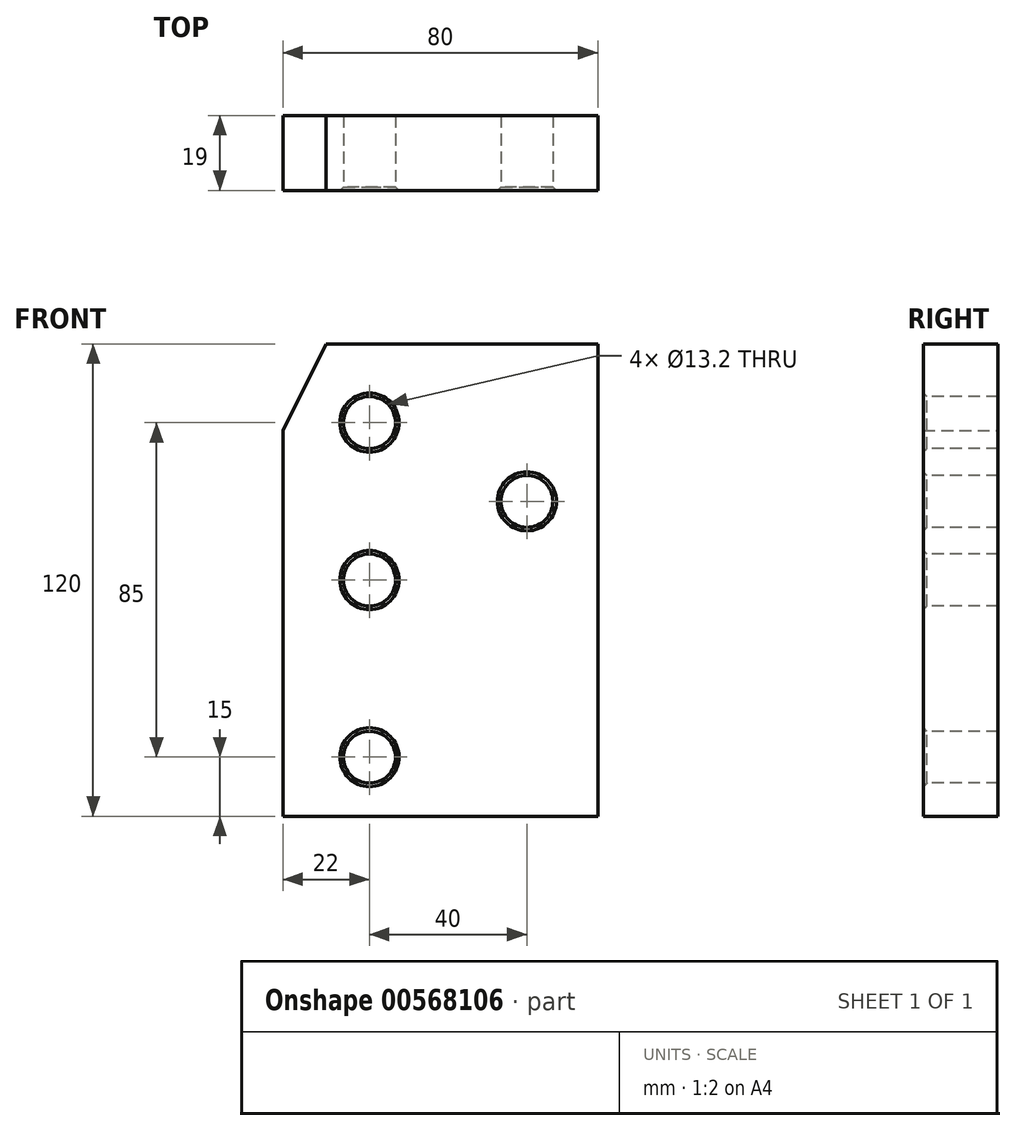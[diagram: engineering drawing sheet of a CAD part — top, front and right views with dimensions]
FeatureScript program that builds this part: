
annotation { "Feature Type Name" : "Feature", "Feature Type Description" : "" }
export const myFeature = defineFeature(function(context is Context, id is Id, definition is map)
    precondition{}
    {
        {
            var Q0;
            Q0=qCreatedBy(makeId("Front.planeOp"),FACE);
            var sketch = newSketch(context, id + "F0", { "sketchPlane" : qUnion([Q0])});
            skLineSegment(sketch, "E0.bottom", {"start": v(0, 0) * mm, "end": v(80, 0) * mm});
            skLineSegment(sketch, "E0.top", {"start": v(11, 120) * mm, "end": v(80, 120) * mm});
            skLineSegment(sketch, "E0.left", {"start": v(0, 0) * mm, "end": v(0, 98) * mm});
            skLineSegment(sketch, "E0.right", {"start": v(80, 0) * mm, "end": v(80, 120) * mm});
            skPoint(sketch, "E1", {"position": v(11, 120) * mm});
            skPoint(sketch, "E2", {"position": v(0, 98) * mm});
            skLineSegment(sketch, "E3", {"start": v(0, 98) * mm, "end": v(11, 120) * mm});
            skPoint(sketch, "E4.orphan", {"position": v(0, 120) * mm});
            skSolve(sketch);
        }
        {
            var Q0;
            Q0 = qSketchRegion(id + "F0", true);
            var Q1;
            Q1=makeQuery(id+"F0.imprint","IMPRINT",FACE,{"disambiguationData":[TD([[makeQuery(id+"F0.imprint","IMPRINT",EDGE,{"derivedFrom":sQuery(id+"F0.wireOp",EDGE,"E0.bottom")}),1.0]])]});
            extrude(context, id + "F1", {"entities" : qUnion([Q0, Q1]), "depth" : 19 * mm, "offsetDistance" : 25 * mm});
        }
        {
            var Q0;
            Q0=makeQuery(id+"F1.opExtrude","CAP_FACE",FACE,{"disambiguationData":[OSD([sQuery(id+"F0.wireOp",EDGE,"E0.bottom"),sQuery(id+"F0.wireOp",EDGE,"E0.top"),sQuery(id+"F0.wireOp",EDGE,"E0.left"),sQuery(id+"F0.wireOp",EDGE,"E0.right")])],"isStart":false});
            var sketch = newSketch(context, id + "F2", { "sketchPlane" : qUnion([Q0])});
            skPoint(sketch, "E5", {"position": v(22, 15) * mm});
            skPoint(sketch, "E6", {"position": v(22, 60) * mm});
            skPoint(sketch, "E7", {"position": v(22, 100) * mm});
            skPoint(sketch, "E8", {"position": v(62, 80) * mm});
            skSolve(sketch);
        }
        {
            var Q0;
            Q0=sQuery(id+"F2.wireOp",VERTEX,"E8");
            var Q1;
            Q1=sQuery(id+"F2.wireOp",VERTEX,"E5");
            var Q2;
            Q2=sQuery(id+"F2.wireOp",VERTEX,"E6");
            var Q3;
            Q3=sQuery(id+"F2.wireOp",VERTEX,"E7");
            var Q4;
            Q4=makeQuery(id+"F1.opExtrude","SWEPT_BODY",BODY,{"disambiguationData":[OSD([sQuery(id+"F0.wireOp",EDGE,"E0.bottom"),sQuery(id+"F0.wireOp",EDGE,"E0.top"),sQuery(id+"F0.wireOp",EDGE,"E0.left"),sQuery(id+"F0.wireOp",EDGE,"E0.right")])]});
            hole(context, id + "F3", {"style" : HoleStyle.C_SINK, "endStyle" : HoleEndStyle.THROUGH, "holeDiameter" : 13.2 * mm, "cSinkDiameter" : 15 * mm, "cSinkAngle" : 90 * degree, "isTappedThrough" : true, "tappedDepth" : 8 * mm, "tapClearance" : 3, "startFromSketch" : true, "locations" : qUnion([Q0, Q1, Q2, Q3]), "scope" : qUnion([Q4])});
        }
    });
